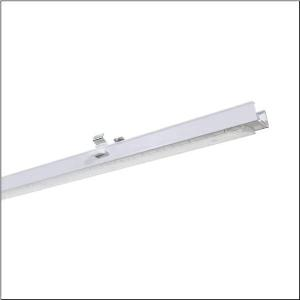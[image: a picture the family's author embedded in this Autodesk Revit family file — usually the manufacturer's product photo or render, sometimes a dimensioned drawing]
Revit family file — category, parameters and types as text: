
# Revit family: trunking_flex_31_51re18mb48b
name_source: partatom
category: Lighting Fixtures
units: mm (PartAtom-declared; Revit-internal decimal feet)

## family parameters
Cut with Voids When Loaded = No
Host = Face
Light Source = No
Part Type = Normal
Room Calculation Point = No
Round Connector Dimension = Use Diameter
Shared = No

## types (1)
- --- (1 x LED, 8000 lm, 50 W, 4000K)
    Apparent Load = 50 VA
    CIE Flux Codes = 71 89 97 97 100
    Color Rendering = 80
    Color Temperature = 4000K
    Default Elevation = 1800 mm
    Description = Trunking Flex 31, luminaire insert, of extruded aluminium section, coated, traffic white (RAL 9016), length: 1.472mm, width: 91mm, height: 53mm, LED rated luminous flux: 8.000lm, light colour: 840, control gear: ON/OFF Multilumen, with system connector: socket, mains connection: 220..240V, AC, 50/60Hz, rated input power: 50W, luminous flux adjustable on luminaire in four steps (4130/5610/6850/8000lm), connected load according to luminous flux setting (25/34/42/50W), primary light control with lens, of plastic, primary optical cover: cover, of PMMA, light emission: direct distribution, protection rating (complete): IP20, insulation class (complete): insulation class I (protective earthing), certification: CE, UKCA, impact resistance: IK02, permissible ambient temperature for indoor applications: -20..+40°C, packaging unit: 1 piece
    Height = 58 mm
    Lamp = 1 x LED
    Lamp Light Flux = 8000 lm
    Lamp Power = 50 W
    Lamp count = 1
    Length = 1472 mm
    Luminous efficacy = 160 lm/W
    Manufacturer = Siteco
    ModVariant = No
    Model = 51RE18MB48B
    Mounting Place = Ceiling
    Mounting Type = Pendant
    Number of Poles = 1
    OnlyDefault = Yes
    Power Factor = 1
    Product Name = Trunking Flex 31
    Product group = luminaire insert
    ProductGroupID = 901
    Protection Class = Protection class I
    Protection Degree = IP 20
    RLX_Detail_Level = 1
    RLX_Emergency_Light_Flux = 0 lm
    RLX_Emergency_Type = 0
    RLX_Emergency_Type_DB = No
    RlxData = <blob elided: 20409 chars, md5=b08b8abf>
    Socket = socket
    Standby Power = 0 W
    System Light Flux = 8000 lm
    System Power = 50 W
    Type Comments = factory setting: luminous flux: 100 % | (ON | ON) | 300 mA
    Type Image = l_1266702.jpg
    URL = http://relux.com
    VarID = @adj_001193
    Voltage = 0 V
    Weight = 0.00 kg
    Width = 65 mm

## geometry (parser evidence)
native form markers: Blend x4, Sweep x9
no freeform markers — native parametric forms only
